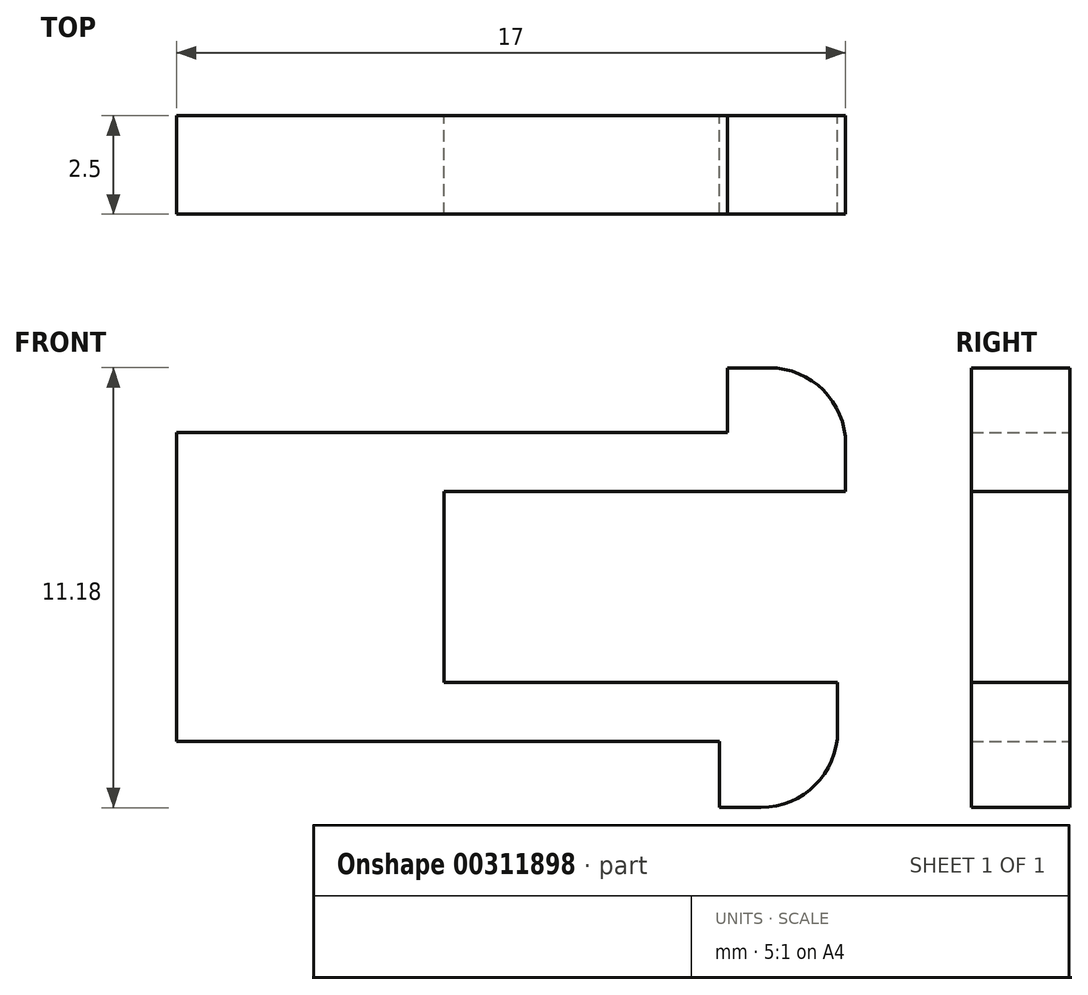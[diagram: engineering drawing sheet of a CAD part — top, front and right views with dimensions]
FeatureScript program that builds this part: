
annotation { "Feature Type Name" : "Feature", "Feature Type Description" : "" }
export const myFeature = defineFeature(function(context is Context, id is Id, definition is map)
    precondition{}
    {
        {
            var Q0;
            Q0=qCreatedBy(makeId("Front.planeOp"),FACE);
            var sketch = newSketch(context, id + "F0", { "sketchPlane" : qUnion([Q0])});
            skLineSegment(sketch, "E0.top", {"start": v(-6.58, -9.03) * mm, "end": v(-16.8, -9.03) * mm});
            skLineSegment(sketch, "E1.bottom", {"start": v(-6.58, -9.03) * mm, "end": v(-3, -9.03) * mm});
            skLineSegment(sketch, "E1.top", {"start": v(-10, -7.53) * mm, "end": v(0, -7.53) * mm});
            skLineSegment(sketch, "E1.right", {"start": v(-1.58, -9.03) * mm, "end": v(0, -7.53) * mm});
            skLineSegment(sketch, "E2.top", {"start": v(-3, -10.72) * mm, "end": v(-1.95, -10.72) * mm});
            skLineSegment(sketch, "E2.left", {"start": v(-3, -9.03) * mm, "end": v(-3, -10.72) * mm});
            skLineSegment(sketch, "E2.right", {"start": v(0, -8.5) * mm, "end": v(0, -8.77) * mm});
            skPoint(sketch, "E3.startSnap0", {"position": v(-4.08, -9.03) * mm});
            skArc(sketch, "E4.filletArc", {"start": v(-1.95, -10.72) * mm, "mid": v(-0.57, -10.15) * mm, "end": v(0, -8.77) * mm});
            skPoint(sketch, "E5.3.end.orphan", {"position": v(-4.08, -9) * mm});
            skLineSegment(sketch, "E6", {"start": v(0, -7.53) * mm, "end": v(0, -8.77) * mm});
            skLineSegment(sketch, "E7.MirrorCS", {"start": v(0.2, -1.76) * mm, "end": v(0.2, -1.49) * mm});
            skLineSegment(sketch, "E8.MirrorCS", {"start": v(0.2, -2.69) * mm, "end": v(0.2, -1.49) * mm});
            skLineSegment(sketch, "E9.MirrorCS", {"start": v(-2.8, 0.46) * mm, "end": v(-1.74, 0.46) * mm});
            skLineSegment(sketch, "E10.MirrorCS", {"start": v(-6.74, -1.19) * mm, "end": v(-2.8, -1.19) * mm});
            skArc(sketch, "E11.MirrorCS", {"start": v(-1.74, 0.46) * mm, "mid": v(-0.37, -0.11) * mm, "end": v(0.2, -1.49) * mm});
            skPoint(sketch, "E12.MirrorP", {"position": v(0, 0.16) * mm});
            skLineSegment(sketch, "E13.MirrorCS", {"start": v(-2.8, -1.19) * mm, "end": v(-2.8, 0.46) * mm});
            skLineSegment(sketch, "E14.MirrorCS", {"start": v(-10, -2.69) * mm, "end": v(0.2, -2.69) * mm});
            skLineSegment(sketch, "E15.MirrorCS", {"start": v(-6.74, -1.19) * mm, "end": v(-16.8, -1.19) * mm});
            skLineSegment(sketch, "E16", {"start": v(-10, -2.69) * mm, "end": v(-10, -7.53) * mm});
            skLineSegment(sketch, "E17", {"start": v(-16.8, -1.19) * mm, "end": v(-16.8, -9.03) * mm});
            skSolve(sketch);
        }
        {
            var Q0;
            Q0=makeQuery(id+"F0.imprint","IMPRINT",FACE,{"disambiguationData":[TD([[makeQuery(id+"F0.imprint","IMPRINT",EDGE,{"derivedFrom":sQuery(id+"F0.wireOp",EDGE,"ZY4yinRf-4u3G-AEFl-IEF8-ajtA5Xp4cYRs.top")}),1.0]])]});
            var Q1;
            Q1=makeQuery(id+"F0.imprint","IMPRINT",FACE,{"disambiguationData":[TD([[makeQuery(id+"F0.imprint","IMPRINT",EDGE,{"derivedFrom":sQuery(id+"F0.wireOp",EDGE,"18d6ff1a-ea28-4fa2-8c59-b0532dc4c62d2.MirrorCS")}),1.0]])]});
            var Q2;
            {var subQ0=sQuery(id+"F0.wireOp",EDGE,"Qrk2VyBV-db8C-d6N0-WsZT-LECVdbsU5BuR.left");Q2=makeQuery(id+"F0.imprint","IMPRINT",FACE,{"disambiguationData":[TD([[makeQuery(id+"F0.imprint","IMPRINT",EDGE,{"derivedFrom":subQ0}),-1.0]])]});}
            var Q3;
            {var subQ0=sQuery(id+"F0.wireOp",EDGE,"18d6ff1a-ea28-4fa2-8c59-b0532dc4c62d6.MirrorCS");Q3=makeQuery(id+"F0.imprint","IMPRINT",FACE,{"disambiguationData":[TD([[makeQuery(id+"F0.imprint","IMPRINT",EDGE,{"derivedFrom":subQ0}),-1.0]])]});}
            var Q4;
            {var subQ0=sQuery(id+"F0.wireOp",EDGE,"Qrk2VyBV-db8C-d6N0-WsZT-LECVdbsU5BuR.left");Q4=makeQuery(id+"F0.imprint","IMPRINT",FACE,{"disambiguationData":[TD([[makeQuery(id+"F0.imprint","IMPRINT",EDGE,{"derivedFrom":subQ0}),1.0]])]});}
            var Q5;
            {var subQ1=sQuery(id+"F0.wireOp",EDGE,"E5.2");Q5=makeQuery(id+"F0.imprint","IMPRINT",FACE,{"disambiguationData":[TD([[makeQuery(id+"F0.imprint","IMPRINT",EDGE,{"derivedFrom":subQ1}),1.0]])]});}
            var Q6;
            {var subQ2=sQuery(id+"F0.wireOp",EDGE,"18d6ff1a-ea28-4fa2-8c59-b0532dc4c62d5.MirrorCS");Q6=makeQuery(id+"F0.imprint","IMPRINT",FACE,{"disambiguationData":[TD([[makeQuery(id+"F0.imprint","IMPRINT",EDGE,{"derivedFrom":subQ2}),-1.0]])]});}
            var Q7;
            Q7=makeQuery(id+"F0.imprint","IMPRINT",FACE,{"disambiguationData":[TD([[makeQuery(id+"F0.imprint","IMPRINT",EDGE,{"derivedFrom":sQuery(id+"F0.wireOp",EDGE,"18d6ff1a-ea28-4fa2-8c59-b0532dc4c62d0.MirrorCS")}),1.0]])]});
            var Q8;
            {var subQ0=sQuery(id+"F0.wireOp",EDGE,"18d6ff1a-ea28-4fa2-8c59-b0532dc4c62d6.MirrorCS");Q8=makeQuery(id+"F0.imprint","IMPRINT",FACE,{"disambiguationData":[TD([[makeQuery(id+"F0.imprint","IMPRINT",EDGE,{"derivedFrom":subQ0}),1.0]])]});}
            var Q9;
            {var subQ3=sQuery(id+"F0.wireOp",EDGE,"UQKBI0hn-hO0K-U3Dy-6t1H-oe98Gb69g6IM.bottom");Q9=makeQuery(id+"F0.imprint","IMPRINT",FACE,{"disambiguationData":[TD([[makeQuery(id+"F0.imprint","IMPRINT",EDGE,{"derivedFrom":subQ3}),-1.0]])]});}
            var Q10;
            Q10=makeQuery(id+"F0.imprint","IMPRINT",FACE,{"disambiguationData":[TD([[makeQuery(id+"F0.imprint","IMPRINT",EDGE,{"derivedFrom":sQuery(id+"F0.wireOp",EDGE,"6zJFjZTr-WSyz-cZE2-Pvhs-ukWOpGhpPHws.bottom")}),1.0]])]});
            var Q11;
            Q11=makeQuery(id+"F0.imprint","IMPRINT",FACE,{"disambiguationData":[TD([[makeQuery(id+"F0.imprint","IMPRINT",EDGE,{"derivedFrom":sQuery(id+"F0.wireOp",EDGE,"6a5c0f3f-3742-448a-8013-d6520f25d6688.MirrorCS")}),-1.0]])]});
            var Q12;
            {var subQ0=sQuery(id+"F0.wireOp",EDGE,"6a5c0f3f-3742-448a-8013-d6520f25d66819.MirrorCS");Q12=makeQuery(id+"F0.imprint","IMPRINT",FACE,{"disambiguationData":[TD([[makeQuery(id+"F0.imprint","IMPRINT",EDGE,{"derivedFrom":subQ0}),1.0]])]});}
            var Q13;
            {var subQ0=sQuery(id+"F0.wireOp",EDGE,"6a5c0f3f-3742-448a-8013-d6520f25d66819.MirrorCS");Q13=makeQuery(id+"F0.imprint","IMPRINT",FACE,{"disambiguationData":[TD([[makeQuery(id+"F0.imprint","IMPRINT",EDGE,{"derivedFrom":subQ0}),-1.0]])]});}
            var Q14;
            Q14=makeQuery(id+"F0.imprint","IMPRINT",FACE,{"disambiguationData":[TD([[makeQuery(id+"F0.imprint","IMPRINT",EDGE,{"derivedFrom":sQuery(id+"F0.wireOp",EDGE,"E9.MirrorCS")}),-1.0]])]});
            var Q15;
            Q15=makeQuery(id+"F0.imprint","IMPRINT",FACE,{"disambiguationData":[TD([[makeQuery(id+"F0.imprint","IMPRINT",EDGE,{"derivedFrom":sQuery(id+"F0.wireOp",EDGE,"6a5c0f3f-3742-448a-8013-d6520f25d6681.MirrorCS")}),1.0]])]});
            var Q16;
            Q16=makeQuery(id+"F0.imprint","IMPRINT",FACE,{"disambiguationData":[TD([[makeQuery(id+"F0.imprint","IMPRINT",EDGE,{"derivedFrom":sQuery(id+"F0.wireOp",EDGE,"6zJFjZTr-WSyz-cZE2-Pvhs-ukWOpGhpPHws.top")}),-1.0]])]});
            var Q17;
            Q17=makeQuery(id+"F0.imprint","IMPRINT",FACE,{"disambiguationData":[TD([[makeQuery(id+"F0.imprint","IMPRINT",EDGE,{"derivedFrom":sQuery(id+"F0.wireOp",EDGE,"E0.top")}),-1.0]])]});
            extrude(context, id + "F1", {"entities" : qUnion([Q0, Q1, Q2, Q3, Q4, Q5, Q6, Q7, Q8, Q9, Q10, Q11, Q12, Q13, Q14, Q15, Q16, Q17]), "depth" : 2.5 * mm});
        }
    });
